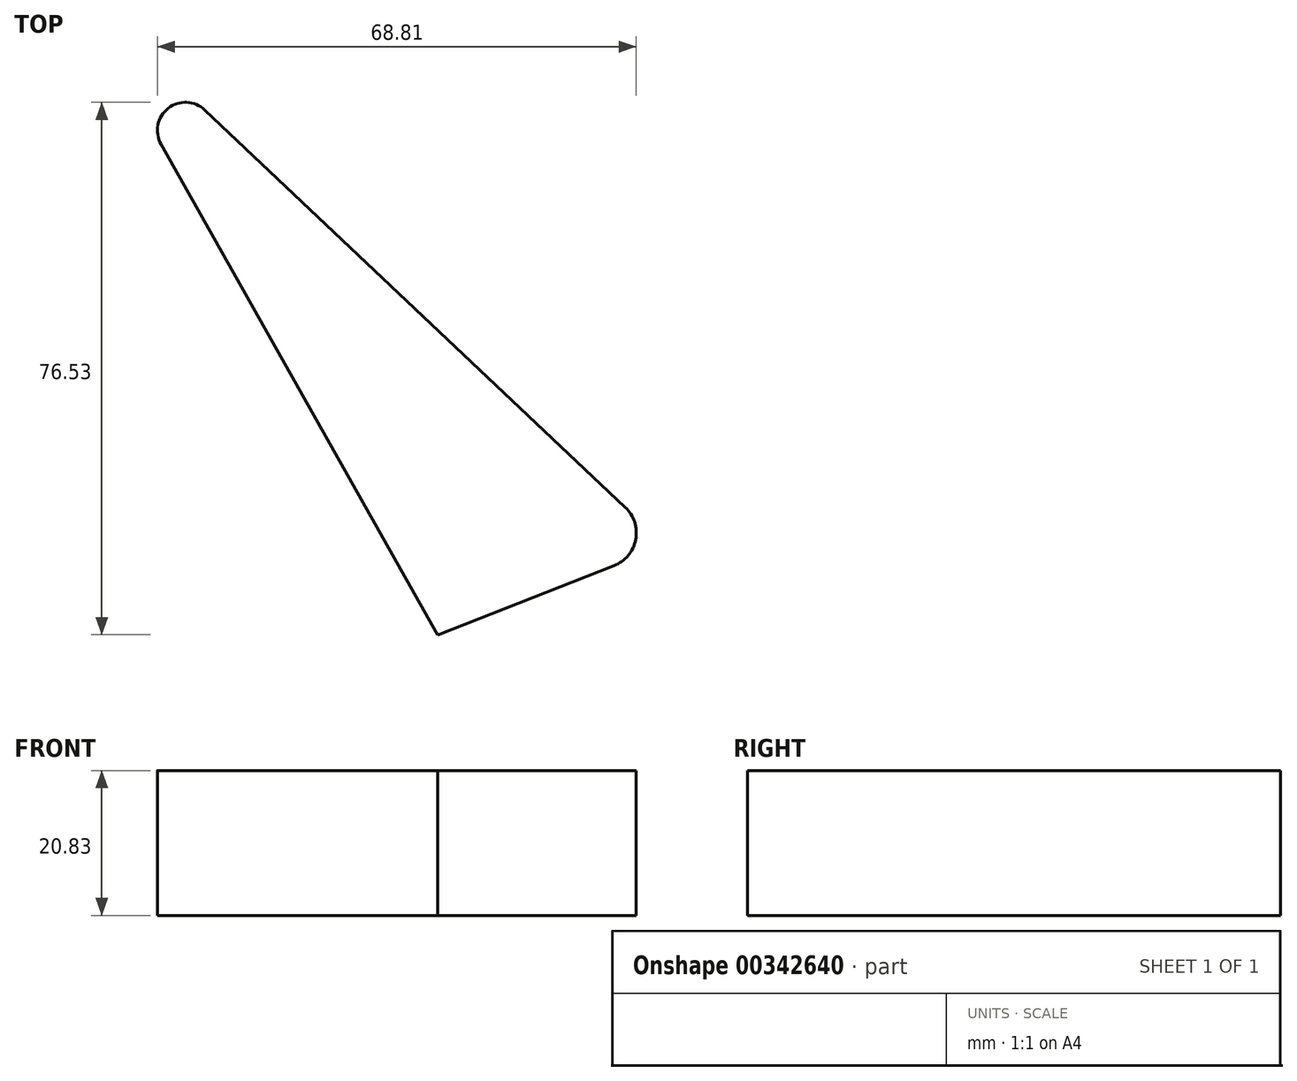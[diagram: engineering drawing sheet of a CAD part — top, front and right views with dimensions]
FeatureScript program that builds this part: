
annotation { "Feature Type Name" : "Feature", "Feature Type Description" : "" }
export const myFeature = defineFeature(function(context is Context, id is Id, definition is map)
    precondition{}
    {
        {
            var Q0;
            Q0=qCreatedBy(makeId("Top.planeOp"),FACE);
            var sketch = newSketch(context, id + "F0", { "sketchPlane" : qUnion([Q0])});
            skLineSegment(sketch, "E0", {"start": v(-96.46, 57.68) * mm, "end": v(-56.74, -12.84) * mm});
            skLineSegment(sketch, "E1", {"start": v(-56.74, -12.84) * mm, "end": v(-31.4, -2.92) * mm});
            skLineSegment(sketch, "E2", {"start": v(-29.76, 5.5) * mm, "end": v(-90.17, 62.6) * mm});
            skPoint(sketch, "E3.visualSharp", {"position": v(-109.54, 80.9) * mm});
            skArc(sketch, "E3.filletArc", {"start": v(-90.17, 62.6) * mm, "mid": v(-95.42, 62.84) * mm, "end": v(-96.46, 57.68) * mm});
            skPoint(sketch, "E4.visualSharp", {"position": v(-23.94, 0) * mm});
            skArc(sketch, "E4.filletArc", {"start": v(-31.4, -2.92) * mm, "mid": v(-28.27, 0.84) * mm, "end": v(-29.76, 5.5) * mm});
            skSolve(sketch);
        }
        {
            var Q0;
            Q0 = qSketchRegion(id + "F0", true);
            extrude(context, id + "F1", {"entities" : qUnion([Q0]), "depth" : 20.83 * mm});
        }
    });
